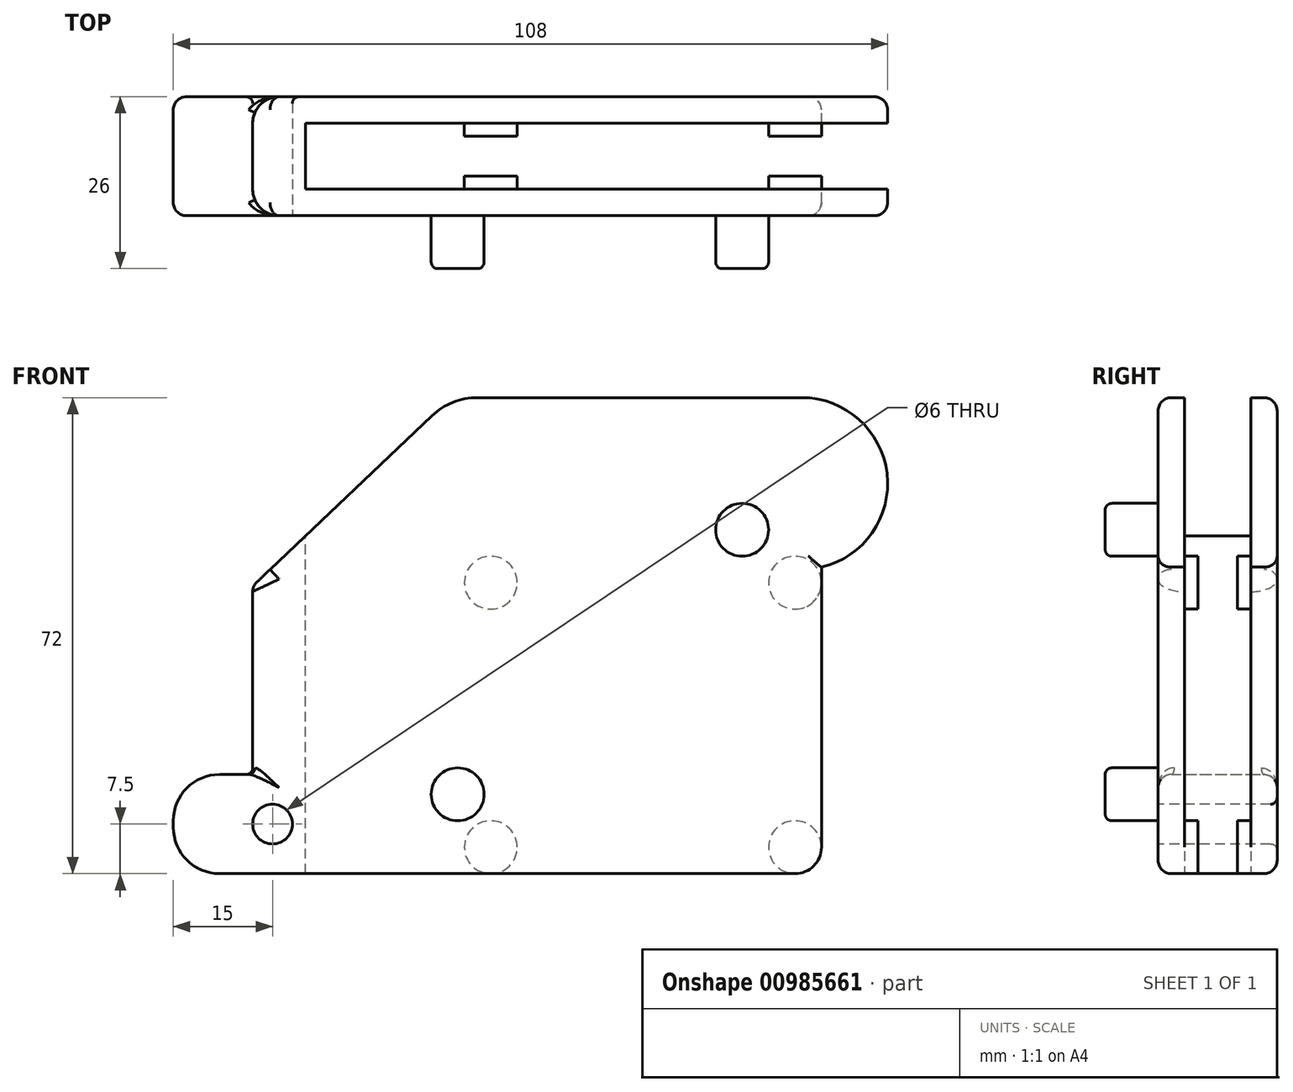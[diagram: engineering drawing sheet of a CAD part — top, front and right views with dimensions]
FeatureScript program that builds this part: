
annotation { "Feature Type Name" : "Feature", "Feature Type Description" : "" }
export const myFeature = defineFeature(function(context is Context, id is Id, definition is map)
    precondition{}
    {
        {
            var Q0;
            Q0=qCreatedBy(makeId("Front.planeOp"),FACE);
            var sketch = newSketch(context, id + "F0", { "sketchPlane" : qUnion([Q0])});
            skLineSegment(sketch, "E0.bottom", {"start": v(-43, 0) * mm, "end": v(39, 0) * mm});
            skLineSegment(sketch, "E0.top", {"start": v(-9, 72) * mm, "end": v(40, 72) * mm});
            skLineSegment(sketch, "E0.left", {"start": v(-43, 15) * mm, "end": v(-43, 43.5) * mm});
            skLineSegment(sketch, "E0.right", {"start": v(43, 4) * mm, "end": v(43, 46.35) * mm});
            skArc(sketch, "E1", {"start": v(43, 46.35) * mm, "mid": v(52.91, 60.51) * mm, "end": v(40, 72) * mm});
            skLineSegment(sketch, "E2.bottom", {"start": v(-43, 0) * mm, "end": v(-48, 0) * mm});
            skLineSegment(sketch, "E2.top", {"start": v(-43, 15) * mm, "end": v(-48, 15) * mm});
            skLineSegment(sketch, "E2.right", {"start": v(-55, 7) * mm, "end": v(-55, 8) * mm});
            skPoint(sketch, "E3.visualSharp", {"position": v(-55, 15) * mm});
            skArc(sketch, "E3.filletArc", {"start": v(-48, 15) * mm, "mid": v(-52.95, 12.95) * mm, "end": v(-55, 8) * mm});
            skPoint(sketch, "E4.visualSharp", {"position": v(-55, 0) * mm});
            skArc(sketch, "E4.filletArc", {"start": v(-55, 7) * mm, "mid": v(-52.95, 2.05) * mm, "end": v(-48, 0) * mm});
            skPoint(sketch, "E5.orphan", {"position": v(43, 72) * mm});
            skLineSegment(sketch, "E6", {"start": v(-43, 43.5) * mm, "end": v(-15.9, 69.25) * mm});
            skPoint(sketch, "E7.orphan", {"position": v(-43, 72) * mm});
            skPoint(sketch, "E8.visualSharp", {"position": v(43, 0) * mm});
            skArc(sketch, "E8.filletArc", {"start": v(39, 0) * mm, "mid": v(41.83, 1.17) * mm, "end": v(43, 4) * mm});
            skPoint(sketch, "E9.0.visualSharp", {"position": v(-13, 72) * mm});
            skArc(sketch, "E9.0.filletArc", {"start": v(-9, 72) * mm, "mid": v(-12.72, 71.29) * mm, "end": v(-15.9, 69.25) * mm});
            skSolve(sketch);
        }
        {
            var Q0;
            Q0 = qSketchRegion(id + "F0", true);
            extrude(context, id + "F1", {"entities" : qUnion([Q0]), "depth" : 18 * mm, "offsetDistance" : 25 * mm, "symmetric" : true});
        }
        {
            var Q0;
            Q0=makeQuery(id+"F1.opExtrude","SWEPT_FACE",FACE,{"disambiguationData":[OSD([sQuery(id+"F0.wireOp",EDGE,"E0.top")])]});
            var sketch = newSketch(context, id + "F2", { "sketchPlane" : qUnion([Q0])});
            skLineSegment(sketch, "E10.bottom", {"start": v(-35, 5) * mm, "end": v(54, 5) * mm});
            skLineSegment(sketch, "E10.top", {"start": v(-35, -5) * mm, "end": v(54, -5) * mm});
            skLineSegment(sketch, "E10.left", {"start": v(-35, 5) * mm, "end": v(-35, -5) * mm});
            skLineSegment(sketch, "E10.right", {"start": v(54, 5) * mm, "end": v(54, -5) * mm});
            skSolve(sketch);
        }
        {
            var Q0;
            Q0 = qSketchRegion(id + "F2", true);
            extrude(context, id + "F3", {"entities" : qUnion([Q0]), "operationType" : NewBodyOperationType.REMOVE, "endBound" : BoundingType.THROUGH_ALL, "oppositeDirection" : true, "depth" : 25 * mm, "offsetDistance" : 25 * mm});
        }
        {
            var Q0;
            Q0=makeQuery(id+"F3.boolean.opBoolean","COPY",FACE,{"derivedFrom":makeQuery(id+"F3.opExtrude","SWEPT_FACE",FACE,{"disambiguationData":[OSD([sQuery(id+"F2.wireOp",EDGE,"E10.bottom")])]})});
            var sketch = newSketch(context, id + "F4", { "sketchPlane" : qUnion([Q0])});
            skCircle(sketch, "E11", {"center": v(-7, 4) * mm, "radius": 4 * mm});
            skCircle(sketch, "E12.0.1.0", {"center": v(-7, 44) * mm, "radius": 4 * mm});
            skCircle(sketch, "E12.1.0.0", {"center": v(39, 4) * mm, "radius": 4 * mm});
            skCircle(sketch, "E12.1.1.0", {"center": v(39, 44) * mm, "radius": 4 * mm});
            skLineSegment(sketch, "E12.direction1", {"start": v(-7, 4) * mm, "end": v(39, 4) * mm, "construction": true});
            skLineSegment(sketch, "E12.direction2", {"start": v(-7, 4) * mm, "end": v(-7, 44) * mm, "construction": true});
            skSolve(sketch);
        }
        {
            var Q0;
            Q0 = qSketchRegion(id + "F4", true);
            extrude(context, id + "F5", {"entities" : qUnion([Q0]), "operationType" : NewBodyOperationType.ADD, "depth" : 10 * mm, "offsetDistance" : 25 * mm});
        }
        {
            var Q0;
            {var subQ2=sQuery(id+"F0.wireOp",EDGE,"E0.top");Q0=makeQuery(id+"F3.boolean.opBoolean","SPLIT",FACE,{"disambiguationData":[TD([makeQuery(id+"F3.opExtrude","SWEPT_FACE",FACE,{"disambiguationData":[OSD([sQuery(id+"F2.wireOp",EDGE,"E10.bottom")])]})])],"derivedFrom":makeQuery(id+"F1.opExtrude","SWEPT_FACE",FACE,{"disambiguationData":[OSD([subQ2])]})});}
            var sketch = newSketch(context, id + "F6", { "sketchPlane" : qUnion([Q0])});
            skLineSegment(sketch, "E13.bottom", {"start": v(-24.99, 3) * mm, "end": v(56.46, 3) * mm});
            skLineSegment(sketch, "E13.top", {"start": v(-24.99, -3) * mm, "end": v(56.46, -3) * mm});
            skLineSegment(sketch, "E13.left", {"start": v(-24.99, 3) * mm, "end": v(-24.99, -3) * mm});
            skLineSegment(sketch, "E13.right", {"start": v(56.46, 3) * mm, "end": v(56.46, -3) * mm});
            skSolve(sketch);
        }
        {
            var Q0;
            Q0 = qSketchRegion(id + "F6", true);
            extrude(context, id + "F7", {"entities" : qUnion([Q0]), "operationType" : NewBodyOperationType.REMOVE, "endBound" : BoundingType.THROUGH_ALL, "oppositeDirection" : true, "depth" : 25 * mm, "offsetDistance" : 25 * mm});
        }
        {
            var Q0;
            Q0=makeQuery(id+"F1.opExtrude","CAP_FACE",FACE,{"disambiguationData":[OSD([sQuery(id+"F0.wireOp",EDGE,"E0.bottom"),sQuery(id+"F0.wireOp",EDGE,"E0.top"),sQuery(id+"F0.wireOp",EDGE,"E0.left"),sQuery(id+"F0.wireOp",EDGE,"E0.right"),sQuery(id+"F0.wireOp",EDGE,"E1"),sQuery(id+"F0.wireOp",EDGE,"E2.bottom"),sQuery(id+"F0.wireOp",EDGE,"E2.top"),sQuery(id+"F0.wireOp",EDGE,"E2.right"),sQuery(id+"F0.wireOp",EDGE,"E3.filletArc"),sQuery(id+"F0.wireOp",EDGE,"E4.filletArc"),sQuery(id+"F0.wireOp",EDGE,"E6"),sQuery(id+"F0.wireOp",EDGE,"E8.filletArc")])],"isStart":false});
            var sketch = newSketch(context, id + "F8", { "sketchPlane" : qUnion([Q0])});
            skCircle(sketch, "E14", {"center": v(-12, 12) * mm, "radius": 4 * mm});
            skCircle(sketch, "E15", {"center": v(31, 52) * mm, "radius": 4 * mm});
            skSolve(sketch);
        }
        {
            var Q0;
            Q0 = qSketchRegion(id + "F8", true);
            extrude(context, id + "F9", {"entities" : qUnion([Q0]), "operationType" : NewBodyOperationType.ADD, "depth" : 8 * mm, "offsetDistance" : 25 * mm});
        }
        {
            var Q0;
            Q0=makeQuery(id+"F9.opExtrude","CAP_EDGE",EDGE,{"disambiguationData":[OSD([sQuery(id+"F8.wireOp",EDGE,"E14")])],"isStart":false});
            var Q1;
            Q1=makeQuery(id+"F9.opExtrude","CAP_EDGE",EDGE,{"disambiguationData":[OSD([sQuery(id+"F8.wireOp",EDGE,"E15")])],"isStart":false});
            fillet(context, id + "F10", {"entities" : qUnion([Q0, Q1]), "radius" : 1 * mm, "tangentPropagation" : true, "allowEdgeOverflow" : false});
        }
        {
            var Q0;
            Q0=makeQuery(id+"F1.opExtrude","CAP_EDGE",EDGE,{"disambiguationData":[OSD([sQuery(id+"F0.wireOp",EDGE,"E6")])],"isStart":false});
            var Q1;
            Q1=makeQuery(id+"F1.opExtrude","CAP_EDGE",EDGE,{"disambiguationData":[OSD([sQuery(id+"F0.wireOp",EDGE,"E0.top")])],"isStart":false});
            var Q2;
            Q2=makeQuery(id+"F1.opExtrude","CAP_EDGE",EDGE,{"disambiguationData":[OSD([sQuery(id+"F0.wireOp",EDGE,"E0.right")])],"isStart":false});
            var Q3;
            Q3=makeQuery(id+"F1.opExtrude","CAP_EDGE",EDGE,{"disambiguationData":[OSD([sQuery(id+"F0.wireOp",EDGE,"E6")])],"isStart":true});
            var Q4;
            Q4=makeQuery(id+"F1.opExtrude","CAP_EDGE",EDGE,{"disambiguationData":[OSD([sQuery(id+"F0.wireOp",EDGE,"E0.bottom"),sQuery(id+"F0.wireOp",EDGE,"E2.bottom")])],"isStart":true});
            var Q5;
            Q5=makeQuery(id+"F1.opExtrude","CAP_EDGE",EDGE,{"disambiguationData":[OSD([sQuery(id+"F0.wireOp",EDGE,"E1")])],"isStart":true});
            var Q6;
            Q6=makeQuery(id+"F1.opExtrude","CAP_EDGE",EDGE,{"disambiguationData":[OSD([sQuery(id+"F0.wireOp",EDGE,"E3.filletArc")])],"isStart":true});
            var Q7;
            Q7=makeQuery(id+"F1.opExtrude","SWEPT_EDGE",EDGE,{"disambiguationData":[OSD([sQuery(id+"F0.wireOp",EDGE,"E0.left"),sQuery(id+"F0.wireOp",EDGE,"E6")])]});
            fillet(context, id + "F11", {"entities" : qUnion([Q0, Q1, Q2, Q3, Q4, Q5, Q6, Q7]), "radius" : 2 * mm, "tangentPropagation" : true, "allowEdgeOverflow" : false});
        }
        {
            var Q0;
            Q0=makeQuery(id+"F1.opExtrude","CAP_EDGE",EDGE,{"disambiguationData":[OSD([sQuery(id+"F0.wireOp",EDGE,"E0.left")])],"isStart":true});
            var Q1;
            Q1=makeQuery(id+"F1.opExtrude","CAP_EDGE",EDGE,{"disambiguationData":[OSD([sQuery(id+"F0.wireOp",EDGE,"E0.left")])],"isStart":false});
            fillet(context, id + "F12", {"entities" : qUnion([Q0, Q1]), "radius" : 4 * mm, "tangentPropagation" : true, "allowEdgeOverflow" : false});
        }
        {
            var Q0;
            Q0=makeQuery(id+"F1.opExtrude","SWEPT_EDGE",EDGE,{"disambiguationData":[OSD([sQuery(id+"F0.wireOp",EDGE,"E0.left"),sQuery(id+"F0.wireOp",EDGE,"E2.top")])]});
            fillet(context, id + "F13", {"entities" : qUnion([Q0]), "radius" : 1 * mm, "tangentPropagation" : true, "allowEdgeOverflow" : false});
        }
        {
            var Q0;
            Q0=makeQuery(id+"F1.opExtrude","CAP_FACE",FACE,{"disambiguationData":[OSD([sQuery(id+"F0.wireOp",EDGE,"E0.bottom"),sQuery(id+"F0.wireOp",EDGE,"E0.top"),sQuery(id+"F0.wireOp",EDGE,"E0.left"),sQuery(id+"F0.wireOp",EDGE,"E0.right"),sQuery(id+"F0.wireOp",EDGE,"E1"),sQuery(id+"F0.wireOp",EDGE,"E2.bottom"),sQuery(id+"F0.wireOp",EDGE,"E2.top"),sQuery(id+"F0.wireOp",EDGE,"E2.right"),sQuery(id+"F0.wireOp",EDGE,"E3.filletArc"),sQuery(id+"F0.wireOp",EDGE,"E4.filletArc"),sQuery(id+"F0.wireOp",EDGE,"E6"),sQuery(id+"F0.wireOp",EDGE,"E8.filletArc")])],"isStart":false});
            var sketch = newSketch(context, id + "F14", { "sketchPlane" : qUnion([Q0])});
            skCircle(sketch, "E16", {"center": v(-40, 7.5) * mm, "radius": 3 * mm});
            skSolve(sketch);
        }
        {
            var Q0;
            Q0 = qSketchRegion(id + "F14", true);
            extrude(context, id + "F15", {"entities" : qUnion([Q0]), "operationType" : NewBodyOperationType.REMOVE, "endBound" : BoundingType.THROUGH_ALL, "oppositeDirection" : true, "depth" : 25 * mm, "offsetDistance" : 25 * mm});
        }
        {
            var Q0;
            Q0=makeQuery(id+"F15.boolean.opBoolean","COPY",EDGE,{"derivedFrom":makeQuery(id+"F15.opExtrude","CAP_EDGE",EDGE,{"disambiguationData":[OSD([sQuery(id+"F14.wireOp",EDGE,"E16")])],"isStart":true})});
            var Q1;
            Q1=makeQuery(id+"F15.boolean.opBoolean","INTERSECT",EDGE,{"derivedFrom":[makeQuery(id+"F1.opExtrude","CAP_FACE",FACE,{"disambiguationData":[OSD([sQuery(id+"F0.wireOp",EDGE,"E0.bottom"),sQuery(id+"F0.wireOp",EDGE,"E0.top"),sQuery(id+"F0.wireOp",EDGE,"E0.left"),sQuery(id+"F0.wireOp",EDGE,"E0.right"),sQuery(id+"F0.wireOp",EDGE,"E1"),sQuery(id+"F0.wireOp",EDGE,"E2.bottom"),sQuery(id+"F0.wireOp",EDGE,"E2.top"),sQuery(id+"F0.wireOp",EDGE,"E2.right"),sQuery(id+"F0.wireOp",EDGE,"E3.filletArc"),sQuery(id+"F0.wireOp",EDGE,"E4.filletArc"),sQuery(id+"F0.wireOp",EDGE,"E6"),sQuery(id+"F0.wireOp",EDGE,"E8.filletArc")])],"isStart":true}),makeQuery(id+"F15.opExtrude","SWEPT_FACE",FACE,{"disambiguationData":[OSD([sQuery(id+"F14.wireOp",EDGE,"E16")])]})]});
            fillet(context, id + "F16", {"entities" : qUnion([Q0, Q1]), "radius" : 1 * mm, "tangentPropagation" : true, "allowEdgeOverflow" : false});
        }
    });
